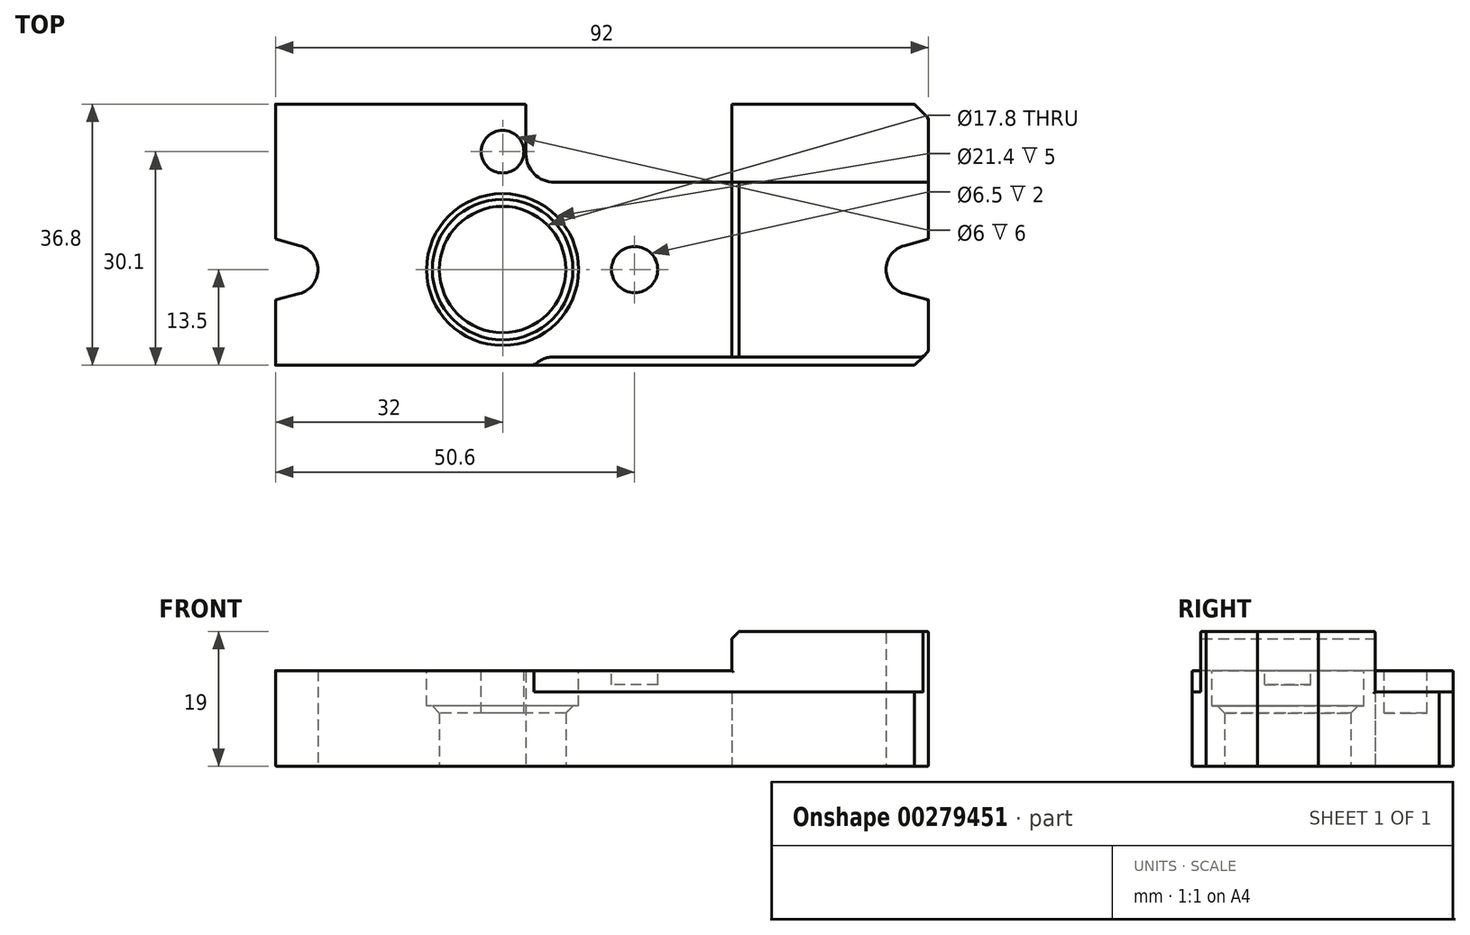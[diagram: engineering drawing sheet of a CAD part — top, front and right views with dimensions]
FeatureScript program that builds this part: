
annotation { "Feature Type Name" : "Feature", "Feature Type Description" : "" }
export const myFeature = defineFeature(function(context is Context, id is Id, definition is map)
    precondition{}
    {
        {
            var Q0;
            Q0=qCreatedBy(makeId("Top.planeOp"),FACE);
            var sketch = newSketch(context, id + "F0", { "sketchPlane" : qUnion([Q0])});
            skLineSegment(sketch, "E0", {"start": v(0, 0) * mm, "end": v(92, 0) * mm});
            skLineSegment(sketch, "E1", {"start": v(92, 0) * mm, "end": v(92, 9.2) * mm});
            skLineSegment(sketch, "E2", {"start": v(92, 36.8) * mm, "end": v(0, 36.8) * mm});
            skLineSegment(sketch, "E3", {"start": v(0, 36.8) * mm, "end": v(0, 17.8) * mm});
            skLineSegment(sketch, "E4", {"start": v(0, 0) * mm, "end": v(0, 9.2) * mm, "construction": true});
            skLineSegment(sketch, "E5", {"start": v(0, 13.5) * mm, "end": v(2.5, 13.5) * mm, "construction": true});
            skLineSegment(sketch, "E6", {"start": v(2.5, 13.5) * mm, "end": v(32, 13.5) * mm, "construction": true});
            skArc(sketch, "E7", {"start": v(3.4, 10.12) * mm, "mid": v(6, 13.5) * mm, "end": v(3.4, 16.88) * mm});
            skCircle(sketch, "E8", {"center": v(32, 13.5) * mm, "radius": 8.9 * mm});
            skCircle(sketch, "E9", {"center": v(32, 13.5) * mm, "radius": 10.7 * mm, "construction": true});
            skArc(sketch, "E10", {"start": v(18.3, 18.25) * mm, "mid": v(17.5, 13.5) * mm, "end": v(18.3, 8.75) * mm});
            skLineSegment(sketch, "E11", {"start": v(0, 0) * mm, "end": v(18.3, 0) * mm, "construction": true});
            skLineSegment(sketch, "E12", {"start": v(18.3, 0) * mm, "end": v(18.3, 8.75) * mm});
            skLineSegment(sketch, "E13.trimOffspring", {"start": v(18.3, 18.25) * mm, "end": v(18.3, 36.8) * mm});
            skLineSegment(sketch, "E14", {"start": v(3.4, 10.12) * mm, "end": v(0, 9.2) * mm});
            skLineSegment(sketch, "E15.MirrorCS", {"start": v(3.4, 16.88) * mm, "end": v(0, 17.8) * mm});
            skLineSegment(sketch, "E16.trimOffspring", {"start": v(0, 9.2) * mm, "end": v(0, 0) * mm});
            skLineSegment(sketch, "E17", {"start": v(32, 13.5) * mm, "end": v(89.5, 13.5) * mm, "construction": true});
            skArc(sketch, "E18", {"start": v(88.6, 16.88) * mm, "mid": v(86, 13.5) * mm, "end": v(88.6, 10.12) * mm});
            skLineSegment(sketch, "E19", {"start": v(88.6, 10.12) * mm, "end": v(92, 9.2) * mm});
            skLineSegment(sketch, "E20.MirrorCS", {"start": v(88.6, 16.88) * mm, "end": v(92, 17.8) * mm});
            skLineSegment(sketch, "E21.trimOffspring", {"start": v(92, 17.8) * mm, "end": v(92, 36.8) * mm});
            skLineSegment(sketch, "E22", {"start": v(0, 0) * mm, "end": v(50.6, 0) * mm, "construction": true});
            skLineSegment(sketch, "E23", {"start": v(50.6, 0) * mm, "end": v(50.6, 13.5) * mm, "construction": true});
            skCircle(sketch, "E24", {"center": v(50.6, 13.5) * mm, "radius": 3.25 * mm, "construction": true});
            skLineSegment(sketch, "E25", {"start": v(0, 0) * mm, "end": v(64.3, 0) * mm, "construction": true});
            skLineSegment(sketch, "E26", {"start": v(64.3, 0) * mm, "end": v(64.3, 36.8) * mm});
            skLineSegment(sketch, "E27", {"start": v(0, 0) * mm, "end": v(0, -2.8) * mm, "construction": true});
            skLineSegment(sketch, "E28", {"start": v(0, -2.8) * mm, "end": v(39.3, -2.8) * mm, "construction": true});
            skLineSegment(sketch, "E29", {"start": v(0, 0) * mm, "end": v(0, 1.2) * mm, "construction": true});
            skLineSegment(sketch, "E30", {"start": v(39.3, 1.2) * mm, "end": v(92, 1.2) * mm});
            skArc(sketch, "E31", {"start": v(39.3, 1.2) * mm, "mid": v(37.75, 0.89) * mm, "end": v(36.44, 0) * mm});
            skLineSegment(sketch, "E32.MirrorCS", {"start": v(39.3, 25.8) * mm, "end": v(92, 25.8) * mm});
            skArc(sketch, "E33.MirrorC", {"start": v(39.3, 25.8) * mm, "mid": v(36.47, 26.97) * mm, "end": v(35.3, 29.8) * mm});
            skLineSegment(sketch, "E34", {"start": v(35.3, 29.8) * mm, "end": v(35.3, 36.8) * mm});
            skPoint(sketch, "E35.orphan", {"position": v(0, 25.8) * mm});
            skLineSegment(sketch, "E36", {"start": v(32, 13.5) * mm, "end": v(32, 30.1) * mm, "construction": true});
            skCircle(sketch, "E37", {"center": v(32, 30.1) * mm, "radius": 3 * mm, "construction": true});
            skSolve(sketch);
        }
        {
            var Q0;
            Q0=qCreatedBy(makeId("Top.planeOp"),FACE);
            cPlane(context, id + "F1", {"entities" : qUnion([Q0]), "cplaneType" : CPlaneType.OFFSET, "offset" : 13.5 * mm, "width" : 150 * mm, "height" : 150 * mm});
        }
        {
            var Q0;
            Q0=qCreatedBy(id+"F1.planeOp",FACE);
            var sketch = newSketch(context, id + "F2", { "sketchPlane" : qUnion([Q0])});
            skCircle(sketch, "E38.0", {"center": v(32, 13.5) * mm, "radius": 10.7 * mm});
            skCircle(sketch, "E39.0", {"center": v(32, 30.1) * mm, "radius": 3 * mm});
            skCircle(sketch, "E40.0", {"center": v(50.6, 13.5) * mm, "radius": 3.25 * mm});
            skArc(sketch, "E41.0.0", {"start": v(18.3, 8.75) * mm, "mid": v(17.5, 13.5) * mm, "end": v(18.3, 18.25) * mm});
            skLineSegment(sketch, "E41.0.1", {"start": v(18.3, 18.25) * mm, "end": v(18.3, 36.8) * mm});
            skLineSegment(sketch, "E41.0.2", {"start": v(18.3, 36.8) * mm, "end": v(0, 36.8) * mm});
            skLineSegment(sketch, "E41.0.3", {"start": v(0, 36.8) * mm, "end": v(0, 17.8) * mm});
            skLineSegment(sketch, "E41.0.4", {"start": v(0, 17.8) * mm, "end": v(3.4, 16.88) * mm});
            skArc(sketch, "E41.0.5", {"start": v(3.4, 16.88) * mm, "mid": v(6, 13.5) * mm, "end": v(3.4, 10.12) * mm});
            skLineSegment(sketch, "E41.0.6", {"start": v(3.4, 10.12) * mm, "end": v(0, 9.2) * mm});
            skLineSegment(sketch, "E41.0.7", {"start": v(0, 9.2) * mm, "end": v(0, 0) * mm});
            skLineSegment(sketch, "E41.0.8", {"start": v(0, 0) * mm, "end": v(18.3, 0) * mm});
            skLineSegment(sketch, "E41.0.9", {"start": v(18.3, 0) * mm, "end": v(18.3, 8.75) * mm});
            skLineSegment(sketch, "E42.0.0", {"start": v(92, 25.8) * mm, "end": v(64.3, 25.8) * mm});
            skLineSegment(sketch, "E42.0.1", {"start": v(64.3, 25.8) * mm, "end": v(64.3, 1.2) * mm});
            skLineSegment(sketch, "E42.0.2", {"start": v(64.3, 1.2) * mm, "end": v(92, 1.2) * mm});
            skLineSegment(sketch, "E42.0.3", {"start": v(92, 1.2) * mm, "end": v(92, 9.2) * mm});
            skLineSegment(sketch, "E42.0.4", {"start": v(92, 9.2) * mm, "end": v(88.6, 10.12) * mm});
            skArc(sketch, "E42.0.5", {"start": v(88.6, 10.12) * mm, "mid": v(86, 13.5) * mm, "end": v(88.6, 16.88) * mm});
            skLineSegment(sketch, "E42.0.6", {"start": v(88.6, 16.88) * mm, "end": v(92, 17.8) * mm});
            skLineSegment(sketch, "E42.0.7", {"start": v(92, 17.8) * mm, "end": v(92, 25.8) * mm});
            skSolve(sketch);
        }
        {
            var Q0;
            {var subQ3=sQuery(id+"F0.wireOp",EDGE,"E3");Q0=makeQuery(id+"F0.imprint","IMPRINT",FACE,{"disambiguationData":[TD([[makeQuery(id+"F0.imprint","IMPRINT",EDGE,{"derivedFrom":subQ3}),1.0]])]});}
            var Q1;
            Q1=makeQuery(id+"F0.imprint","IMPRINT",FACE,{"disambiguationData":[TD([[makeQuery(id+"F0.imprint","IMPRINT",EDGE,{"derivedFrom":sQuery(id+"F0.wireOp",EDGE,"E8")}),-1.0]])]});
            var Q2;
            Q2=makeQuery(id+"F0.imprint","IMPRINT",FACE,{"disambiguationData":[TD([[makeQuery(id+"F0.imprint","IMPRINT",EDGE,{"derivedFrom":sQuery(id+"F0.wireOp",EDGE,"E18")}),-1.0]])]});
            extrude(context, id + "F3", {"entities" : qUnion([Q0, Q1, Q2]), "depth" : 13.5 * mm});
        }
        {
            var Q0;
            {var subQ0=sQuery(id+"F0.wireOp",EDGE,"E1");var subQ1=sQuery(id+"F0.wireOp",EDGE,"E0");var subQ2=makeQuery(id+"F0.imprint","INTERSECT",VERTEX,{"derivedFrom":[subQ1,subQ0]});Q0=makeQuery(id+"F0.imprint","IMPRINT",FACE,{"disambiguationData":[TD([[makeQuery(id+"F0.imprint","IMPRINT",EDGE,{"disambiguationData":[TD([[subQ2,1.0]])],"derivedFrom":subQ1}),1.0]])]});}
            var Q1;
            {var subQ3=sQuery(id+"F0.wireOp",EDGE,"E31");Q1=makeQuery(id+"F0.imprint","IMPRINT",FACE,{"disambiguationData":[TD([[makeQuery(id+"F0.imprint","IMPRINT",EDGE,{"derivedFrom":subQ3}),1.0]])]});}
            var Q2;
            {var subQ0=sQuery(id+"F0.wireOp",EDGE,"E33.MirrorC");Q2=makeQuery(id+"F0.imprint","IMPRINT",FACE,{"disambiguationData":[TD([[makeQuery(id+"F0.imprint","IMPRINT",EDGE,{"derivedFrom":subQ0}),-1.0]])]});}
            var Q3;
            {var subQ0=sQuery(id+"F0.wireOp",EDGE,"E21.trimOffspring");var subQ1=sQuery(id+"F0.wireOp",EDGE,"E2");var subQ2=makeQuery(id+"F0.imprint","INTERSECT",VERTEX,{"derivedFrom":[subQ1,subQ0]});Q3=makeQuery(id+"F0.imprint","IMPRINT",FACE,{"disambiguationData":[TD([[makeQuery(id+"F0.imprint","IMPRINT",EDGE,{"disambiguationData":[TD([[subQ2,-1.0]])],"derivedFrom":subQ1}),1.0]])]});}
            extrude(context, id + "F4", {"entities" : qUnion([Q0, Q1, Q2, Q3]), "operationType" : NewBodyOperationType.ADD, "depth" : 10.5 * mm});
        }
        {
            var Q0;
            Q0=makeQuery(id+"F2.imprint","IMPRINT",FACE,{"disambiguationData":[TD([[makeQuery(id+"F2.imprint","IMPRINT",EDGE,{"derivedFrom":sQuery(id+"F2.wireOp",EDGE,"E38.0")}),1.0]])]});
            extrude(context, id + "F5", {"entities" : qUnion([Q0]), "operationType" : NewBodyOperationType.REMOVE, "oppositeDirection" : true, "depth" : 5 * mm});
        }
        {
            var Q0;
            Q0=makeQuery(id+"F2.imprint","IMPRINT",FACE,{"disambiguationData":[TD([[makeQuery(id+"F2.imprint","IMPRINT",EDGE,{"derivedFrom":sQuery(id+"F2.wireOp",EDGE,"E40.0")}),1.0]])]});
            extrude(context, id + "F6", {"entities" : qUnion([Q0]), "operationType" : NewBodyOperationType.REMOVE, "oppositeDirection" : true, "depth" : 2 * mm});
        }
        {
            var Q0;
            Q0=makeQuery(id+"F2.imprint","IMPRINT",FACE,{"disambiguationData":[TD([[makeQuery(id+"F2.imprint","IMPRINT",EDGE,{"derivedFrom":sQuery(id+"F2.wireOp",EDGE,"E39.0")}),1.0]])]});
            extrude(context, id + "F7", {"entities" : qUnion([Q0]), "operationType" : NewBodyOperationType.REMOVE, "oppositeDirection" : true, "depth" : 6 * mm});
        }
        {
            var Q0;
            Q0=makeQuery(id+"F2.imprint","IMPRINT",FACE,{"disambiguationData":[TD([[makeQuery(id+"F2.imprint","IMPRINT",EDGE,{"derivedFrom":sQuery(id+"F2.wireOp",EDGE,"E41.0.0")}),1.0]])]});
            var Q1;
            Q1=makeQuery(id+"F2.imprint","IMPRINT",FACE,{"disambiguationData":[TD([[makeQuery(id+"F2.imprint","IMPRINT",EDGE,{"derivedFrom":sQuery(id+"F2.wireOp",EDGE,"E42.0.0")}),1.0]])]});
            extrude(context, id + "F8", {"entities" : qUnion([Q0, Q1]), "operationType" : NewBodyOperationType.ADD, "depth" : 5.5 * mm});
        }
        {
            var Q0;
            Q0=makeQuery(id+"F5.boolean.opBoolean","INTERSECT",EDGE,{"derivedFrom":[makeQuery(id+"F3.opExtrude","SWEPT_FACE",FACE,{"disambiguationData":[OSD([sQuery(id+"F0.wireOp",EDGE,"E8")])]}),makeQuery(id+"F5.opExtrude","CAP_FACE",FACE,{"disambiguationData":[OSD([sQuery(id+"F2.wireOp",EDGE,"E38.0")])],"isStart":false})]});
            var Q1;
            Q1=makeQuery(id+"F8.opExtrude","CAP_EDGE",EDGE,{"disambiguationData":[OSD([sQuery(id+"F2.wireOp",EDGE,"E41.0.1")])],"isStart":false});
            var Q2;
            Q2=makeQuery(id+"F8.opExtrude","CAP_EDGE",EDGE,{"disambiguationData":[OSD([sQuery(id+"F2.wireOp",EDGE,"E42.0.1")])],"isStart":false});
            chamfer(context, id + "F9", {"entities" : qUnion([Q0, Q1, Q2]), "width" : 1 * mm, "tangentPropagation" : true});
        }
        {
            var Q0;
            Q0=makeQuery(id+"F4.opExtrude","SWEPT_EDGE",EDGE,{"disambiguationData":[OSD([sQuery(id+"F0.wireOp",EDGE,"E0"),sQuery(id+"F0.wireOp",EDGE,"E1")])]});
            var Q1;
            Q1=makeQuery(id+"F4.opExtrude","SWEPT_EDGE",EDGE,{"disambiguationData":[OSD([sQuery(id+"F0.wireOp",EDGE,"E2"),sQuery(id+"F0.wireOp",EDGE,"E21.trimOffspring")])]});
            var Q2;
            Q2=makeQuery(id+"F8.boolean.opBoolean","MERGE",EDGE,{"derivedFrom":[makeQuery(id+"F3.opExtrude","SWEPT_EDGE",EDGE,{"disambiguationData":[OSD([sQuery(id+"F0.wireOp",EDGE,"E2"),sQuery(id+"F0.wireOp",EDGE,"E3")])]}),makeQuery(id+"F8.opExtrude","SWEPT_EDGE",EDGE,{"disambiguationData":[OSD([sQuery(id+"F2.wireOp",EDGE,"E41.0.2"),sQuery(id+"F2.wireOp",EDGE,"E41.0.3")])]})]});
            var Q3;
            Q3=makeQuery(id+"F8.boolean.opBoolean","MERGE",EDGE,{"derivedFrom":[makeQuery(id+"F3.opExtrude","SWEPT_EDGE",EDGE,{"disambiguationData":[OSD([sQuery(id+"F0.wireOp",EDGE,"E0"),sQuery(id+"F0.wireOp",EDGE,"E16.trimOffspring")])]}),makeQuery(id+"F8.opExtrude","SWEPT_EDGE",EDGE,{"disambiguationData":[OSD([sQuery(id+"F2.wireOp",EDGE,"E41.0.7"),sQuery(id+"F2.wireOp",EDGE,"E41.0.8")])]})]});
            chamfer(context, id + "F10", {"entities" : qUnion([Q0, Q1, Q2, Q3]), "width" : 2 * mm, "tangentPropagation" : true});
        }
        {
            var Q0;
            {var subQ0=sQuery(id+"F2.wireOp",EDGE,"E41.0.8");var subQ1=sQuery(id+"F2.wireOp",EDGE,"E41.0.7");Q0=makeQuery(id+"F10.opChamfer","BLEND_EDGE",EDGE,{"blendedFrom":[makeQuery(id+"F8.boolean.opBoolean","MERGE",EDGE,{"derivedFrom":[makeQuery(id+"F3.opExtrude","SWEPT_EDGE",EDGE,{"disambiguationData":[OSD([sQuery(id+"F0.wireOp",EDGE,"E0"),sQuery(id+"F0.wireOp",EDGE,"E16.trimOffspring")])]}),makeQuery(id+"F8.opExtrude","SWEPT_EDGE",EDGE,{"disambiguationData":[OSD([subQ1,subQ0])]})]}),makeQuery(id+"F8.opExtrude","CAP_FACE",FACE,{"disambiguationData":[OSD([sQuery(id+"F2.wireOp",EDGE,"E41.0.0"),sQuery(id+"F2.wireOp",EDGE,"E41.0.1"),sQuery(id+"F2.wireOp",EDGE,"E41.0.2"),sQuery(id+"F2.wireOp",EDGE,"E41.0.3"),sQuery(id+"F2.wireOp",EDGE,"E41.0.4"),sQuery(id+"F2.wireOp",EDGE,"E41.0.5"),sQuery(id+"F2.wireOp",EDGE,"E41.0.6"),subQ1,subQ0,sQuery(id+"F2.wireOp",EDGE,"E41.0.9")])],"isStart":false})],"blendedInto":[makeQuery(id+"F8.opExtrude","CAP_FACE",FACE,{"disambiguationData":[OSD([sQuery(id+"F2.wireOp",EDGE,"E41.0.0"),sQuery(id+"F2.wireOp",EDGE,"E41.0.1"),sQuery(id+"F2.wireOp",EDGE,"E41.0.2"),sQuery(id+"F2.wireOp",EDGE,"E41.0.3"),sQuery(id+"F2.wireOp",EDGE,"E41.0.4"),sQuery(id+"F2.wireOp",EDGE,"E41.0.5"),sQuery(id+"F2.wireOp",EDGE,"E41.0.6"),subQ1,subQ0,sQuery(id+"F2.wireOp",EDGE,"E41.0.9")])],"isStart":false})]});}
            var Q1;
            Q1=makeQuery(id+"F8.opExtrude","CAP_EDGE",EDGE,{"disambiguationData":[OSD([sQuery(id+"F2.wireOp",EDGE,"E41.0.7")])],"isStart":false});
            var Q2;
            Q2=makeQuery(id+"F8.opExtrude","CAP_EDGE",EDGE,{"disambiguationData":[OSD([sQuery(id+"F2.wireOp",EDGE,"E41.0.6")])],"isStart":false});
            var Q3;
            Q3=makeQuery(id+"F8.opExtrude","CAP_EDGE",EDGE,{"disambiguationData":[OSD([sQuery(id+"F2.wireOp",EDGE,"E41.0.5")])],"isStart":false});
            var Q4;
            Q4=makeQuery(id+"F8.opExtrude","CAP_EDGE",EDGE,{"disambiguationData":[OSD([sQuery(id+"F2.wireOp",EDGE,"E41.0.3")])],"isStart":false});
            var Q5;
            Q5=makeQuery(id+"F8.opExtrude","CAP_EDGE",EDGE,{"disambiguationData":[OSD([sQuery(id+"F2.wireOp",EDGE,"E41.0.4")])],"isStart":false});
            var Q6;
            {var subQ0=sQuery(id+"F2.wireOp",EDGE,"E41.0.3");var subQ1=sQuery(id+"F2.wireOp",EDGE,"E41.0.2");Q6=makeQuery(id+"F10.opChamfer","BLEND_EDGE",EDGE,{"blendedFrom":[makeQuery(id+"F8.boolean.opBoolean","MERGE",EDGE,{"derivedFrom":[makeQuery(id+"F3.opExtrude","SWEPT_EDGE",EDGE,{"disambiguationData":[OSD([sQuery(id+"F0.wireOp",EDGE,"E2"),sQuery(id+"F0.wireOp",EDGE,"E3")])]}),makeQuery(id+"F8.opExtrude","SWEPT_EDGE",EDGE,{"disambiguationData":[OSD([subQ1,subQ0])]})]}),makeQuery(id+"F8.opExtrude","CAP_FACE",FACE,{"disambiguationData":[OSD([sQuery(id+"F2.wireOp",EDGE,"E41.0.0"),sQuery(id+"F2.wireOp",EDGE,"E41.0.1"),subQ1,subQ0,sQuery(id+"F2.wireOp",EDGE,"E41.0.4"),sQuery(id+"F2.wireOp",EDGE,"E41.0.5"),sQuery(id+"F2.wireOp",EDGE,"E41.0.6"),sQuery(id+"F2.wireOp",EDGE,"E41.0.7"),sQuery(id+"F2.wireOp",EDGE,"E41.0.8"),sQuery(id+"F2.wireOp",EDGE,"E41.0.9")])],"isStart":false})],"blendedInto":[makeQuery(id+"F8.opExtrude","CAP_FACE",FACE,{"disambiguationData":[OSD([sQuery(id+"F2.wireOp",EDGE,"E41.0.0"),sQuery(id+"F2.wireOp",EDGE,"E41.0.1"),subQ1,subQ0,sQuery(id+"F2.wireOp",EDGE,"E41.0.4"),sQuery(id+"F2.wireOp",EDGE,"E41.0.5"),sQuery(id+"F2.wireOp",EDGE,"E41.0.6"),sQuery(id+"F2.wireOp",EDGE,"E41.0.7"),sQuery(id+"F2.wireOp",EDGE,"E41.0.8"),sQuery(id+"F2.wireOp",EDGE,"E41.0.9")])],"isStart":false})]});}
            var Q7;
            Q7=makeQuery(id+"F8.opExtrude","CAP_EDGE",EDGE,{"disambiguationData":[OSD([sQuery(id+"F2.wireOp",EDGE,"E41.0.2")])],"isStart":false});
            var Q8;
            {var subQ0=sQuery(id+"F0.wireOp",EDGE,"E2");Q8=makeQuery(id+"F9.opChamfer","BLEND_EDGE",EDGE,{"blendedFrom":[makeQuery(id+"F8.opExtrude","CAP_EDGE",EDGE,{"disambiguationData":[OSD([sQuery(id+"F2.wireOp",EDGE,"E41.0.1")])],"isStart":false}),makeQuery(id+"F8.boolean.opBoolean","MERGE",FACE,{"derivedFrom":[makeQuery(id+"F4.boolean.opBoolean","MERGE",FACE,{"derivedFrom":[makeQuery(id+"F3.opExtrude","SWEPT_FACE",FACE,{"disambiguationData":[OSD([subQ0])]}),makeQuery(id+"F4.opExtrude","SWEPT_FACE",FACE,{"disambiguationData":[OSD([subQ0])]})]}),makeQuery(id+"F8.opExtrude","SWEPT_FACE",FACE,{"disambiguationData":[OSD([sQuery(id+"F2.wireOp",EDGE,"E41.0.2")])]})]})],"blendedInto":[makeQuery(id+"F8.boolean.opBoolean","MERGE",FACE,{"derivedFrom":[makeQuery(id+"F4.boolean.opBoolean","MERGE",FACE,{"derivedFrom":[makeQuery(id+"F3.opExtrude","SWEPT_FACE",FACE,{"disambiguationData":[OSD([subQ0])]}),makeQuery(id+"F4.opExtrude","SWEPT_FACE",FACE,{"disambiguationData":[OSD([subQ0])]})]}),makeQuery(id+"F8.opExtrude","SWEPT_FACE",FACE,{"disambiguationData":[OSD([sQuery(id+"F2.wireOp",EDGE,"E41.0.2")])]})]})]});}
            var Q9;
            Q9=makeQuery(id+"F8.opExtrude","SWEPT_EDGE",EDGE,{"disambiguationData":[OSD([sQuery(id+"F2.wireOp",EDGE,"E41.0.1"),sQuery(id+"F2.wireOp",EDGE,"E41.0.2")])]});
            var Q10;
            Q10=makeQuery(id+"F3.opExtrude","CAP_EDGE",EDGE,{"disambiguationData":[OSD([sQuery(id+"F0.wireOp",EDGE,"E2")])],"isStart":false});
            var Q11;
            Q11=makeQuery(id+"F3.opExtrude","SWEPT_EDGE",EDGE,{"disambiguationData":[OSD([sQuery(id+"F0.wireOp",EDGE,"E2"),sQuery(id+"F0.wireOp",EDGE,"E34")])]});
            var Q12;
            Q12=makeQuery(id+"F4.opExtrude","CAP_EDGE",EDGE,{"disambiguationData":[OSD([sQuery(id+"F0.wireOp",EDGE,"E2")])],"isStart":false});
            var Q13;
            {var subQ0=sQuery(id+"F0.wireOp",EDGE,"E21.trimOffspring");var subQ1=sQuery(id+"F0.wireOp",EDGE,"E2");Q13=makeQuery(id+"F10.opChamfer","BLEND_EDGE",EDGE,{"blendedFrom":[makeQuery(id+"F4.opExtrude","SWEPT_EDGE",EDGE,{"disambiguationData":[OSD([subQ1,subQ0])]}),makeQuery(id+"F4.opExtrude","CAP_FACE",FACE,{"disambiguationData":[OSD([subQ1,subQ0,sQuery(id+"F0.wireOp",EDGE,"E32.MirrorCS"),sQuery(id+"F0.wireOp",EDGE,"E33.MirrorC"),sQuery(id+"F0.wireOp",EDGE,"E34")])],"isStart":false})],"blendedInto":[makeQuery(id+"F4.opExtrude","CAP_FACE",FACE,{"disambiguationData":[OSD([subQ1,subQ0,sQuery(id+"F0.wireOp",EDGE,"E32.MirrorCS"),sQuery(id+"F0.wireOp",EDGE,"E33.MirrorC"),sQuery(id+"F0.wireOp",EDGE,"E34")])],"isStart":false})]});}
            var Q14;
            Q14=makeQuery(id+"F4.opExtrude","CAP_EDGE",EDGE,{"disambiguationData":[OSD([sQuery(id+"F0.wireOp",EDGE,"E21.trimOffspring")])],"isStart":false});
            var Q15;
            Q15=makeQuery(id+"F8.boolean.opBoolean","MERGE",EDGE,{"derivedFrom":[makeQuery(id+"F3.opExtrude","SWEPT_EDGE",EDGE,{"disambiguationData":[OSD([sQuery(id+"F0.wireOp",EDGE,"E21.trimOffspring"),sQuery(id+"F0.wireOp",EDGE,"E32.MirrorCS")])]}),makeQuery(id+"F8.opExtrude","SWEPT_EDGE",EDGE,{"disambiguationData":[OSD([sQuery(id+"F2.wireOp",EDGE,"E42.0.0"),sQuery(id+"F2.wireOp",EDGE,"E42.0.7")])]})]});
            var Q16;
            Q16=makeQuery(id+"F8.opExtrude","CAP_EDGE",EDGE,{"disambiguationData":[OSD([sQuery(id+"F2.wireOp",EDGE,"E42.0.0")])],"isStart":false});
            var Q17;
            Q17=makeQuery(id+"F8.opExtrude","CAP_EDGE",EDGE,{"disambiguationData":[OSD([sQuery(id+"F2.wireOp",EDGE,"E42.0.2")])],"isStart":false});
            var Q18;
            Q18=makeQuery(id+"F10.opChamfer","BLEND_EDGE",EDGE,{"blendedFrom":[makeQuery(id+"F4.opExtrude","SWEPT_EDGE",EDGE,{"disambiguationData":[OSD([sQuery(id+"F0.wireOp",EDGE,"E0"),sQuery(id+"F0.wireOp",EDGE,"E1")])]}),makeQuery(id+"F8.opExtrude","CAP_FACE",FACE,{"disambiguationData":[OSD([sQuery(id+"F2.wireOp",EDGE,"E42.0.0"),sQuery(id+"F2.wireOp",EDGE,"E42.0.1"),sQuery(id+"F2.wireOp",EDGE,"E42.0.2"),sQuery(id+"F2.wireOp",EDGE,"E42.0.3"),sQuery(id+"F2.wireOp",EDGE,"E42.0.4"),sQuery(id+"F2.wireOp",EDGE,"E42.0.5"),sQuery(id+"F2.wireOp",EDGE,"E42.0.6"),sQuery(id+"F2.wireOp",EDGE,"E42.0.7")])],"isStart":false})],"blendedInto":[makeQuery(id+"F8.opExtrude","CAP_FACE",FACE,{"disambiguationData":[OSD([sQuery(id+"F2.wireOp",EDGE,"E42.0.0"),sQuery(id+"F2.wireOp",EDGE,"E42.0.1"),sQuery(id+"F2.wireOp",EDGE,"E42.0.2"),sQuery(id+"F2.wireOp",EDGE,"E42.0.3"),sQuery(id+"F2.wireOp",EDGE,"E42.0.4"),sQuery(id+"F2.wireOp",EDGE,"E42.0.5"),sQuery(id+"F2.wireOp",EDGE,"E42.0.6"),sQuery(id+"F2.wireOp",EDGE,"E42.0.7")])],"isStart":false})]});
            var Q19;
            Q19=makeQuery(id+"F8.opExtrude","CAP_EDGE",EDGE,{"disambiguationData":[OSD([sQuery(id+"F2.wireOp",EDGE,"E42.0.3")])],"isStart":false});
            var Q20;
            Q20=makeQuery(id+"F8.opExtrude","CAP_EDGE",EDGE,{"disambiguationData":[OSD([sQuery(id+"F2.wireOp",EDGE,"E42.0.4")])],"isStart":false});
            var Q21;
            Q21=makeQuery(id+"F8.opExtrude","CAP_EDGE",EDGE,{"disambiguationData":[OSD([sQuery(id+"F2.wireOp",EDGE,"E42.0.5")])],"isStart":false});
            var Q22;
            Q22=makeQuery(id+"F8.opExtrude","CAP_EDGE",EDGE,{"disambiguationData":[OSD([sQuery(id+"F2.wireOp",EDGE,"E42.0.7")])],"isStart":false});
            var Q23;
            Q23=makeQuery(id+"F8.opExtrude","SWEPT_EDGE",EDGE,{"disambiguationData":[OSD([sQuery(id+"F2.wireOp",EDGE,"E42.0.1"),sQuery(id+"F2.wireOp",EDGE,"E42.0.2")])]});
            var Q24;
            Q24=makeQuery(id+"F3.opExtrude","CAP_EDGE",EDGE,{"disambiguationData":[OSD([sQuery(id+"F0.wireOp",EDGE,"E30")])],"isStart":false});
            var Q25;
            Q25=makeQuery(id+"F3.opExtrude","CAP_EDGE",EDGE,{"disambiguationData":[OSD([sQuery(id+"F0.wireOp",EDGE,"E0")])],"isStart":false});
            var Q26;
            Q26=makeQuery(id+"F8.opExtrude","SWEPT_EDGE",EDGE,{"disambiguationData":[OSD([sQuery(id+"F2.wireOp",EDGE,"E41.0.8"),sQuery(id+"F2.wireOp",EDGE,"E41.0.9")])]});
            var Q27;
            {var subQ0=sQuery(id+"F0.wireOp",EDGE,"E0");Q27=makeQuery(id+"F9.opChamfer","BLEND_EDGE",EDGE,{"blendedFrom":[makeQuery(id+"F8.opExtrude","CAP_EDGE",EDGE,{"disambiguationData":[OSD([sQuery(id+"F2.wireOp",EDGE,"E41.0.1")])],"isStart":false}),makeQuery(id+"F8.boolean.opBoolean","MERGE",FACE,{"derivedFrom":[makeQuery(id+"F4.boolean.opBoolean","MERGE",FACE,{"derivedFrom":[makeQuery(id+"F3.opExtrude","SWEPT_FACE",FACE,{"disambiguationData":[OSD([subQ0])]}),makeQuery(id+"F4.opExtrude","SWEPT_FACE",FACE,{"disambiguationData":[OSD([subQ0])]})]}),makeQuery(id+"F8.opExtrude","SWEPT_FACE",FACE,{"disambiguationData":[OSD([sQuery(id+"F2.wireOp",EDGE,"E41.0.8")])]})]})],"blendedInto":[makeQuery(id+"F8.boolean.opBoolean","MERGE",FACE,{"derivedFrom":[makeQuery(id+"F4.boolean.opBoolean","MERGE",FACE,{"derivedFrom":[makeQuery(id+"F3.opExtrude","SWEPT_FACE",FACE,{"disambiguationData":[OSD([subQ0])]}),makeQuery(id+"F4.opExtrude","SWEPT_FACE",FACE,{"disambiguationData":[OSD([subQ0])]})]}),makeQuery(id+"F8.opExtrude","SWEPT_FACE",FACE,{"disambiguationData":[OSD([sQuery(id+"F2.wireOp",EDGE,"E41.0.8")])]})]})]});}
            var Q28;
            Q28=makeQuery(id+"F8.opExtrude","CAP_EDGE",EDGE,{"disambiguationData":[OSD([sQuery(id+"F2.wireOp",EDGE,"E41.0.8")])],"isStart":false});
            var Q29;
            Q29=makeQuery(id+"F8.opExtrude","SWEPT_EDGE",EDGE,{"disambiguationData":[OSD([sQuery(id+"F2.wireOp",EDGE,"E42.0.0"),sQuery(id+"F2.wireOp",EDGE,"E42.0.1")])]});
            var Q30;
            Q30=makeQuery(id+"F9.opChamfer","BLEND_EDGE",EDGE,{"blendedFrom":[makeQuery(id+"F8.opExtrude","CAP_EDGE",EDGE,{"disambiguationData":[OSD([sQuery(id+"F2.wireOp",EDGE,"E42.0.1")])],"isStart":false}),makeQuery(id+"F8.boolean.opBoolean","MERGE",FACE,{"derivedFrom":[makeQuery(id+"F3.opExtrude","SWEPT_FACE",FACE,{"disambiguationData":[OSD([sQuery(id+"F0.wireOp",EDGE,"E32.MirrorCS")])]}),makeQuery(id+"F8.opExtrude","SWEPT_FACE",FACE,{"disambiguationData":[OSD([sQuery(id+"F2.wireOp",EDGE,"E42.0.0")])]})]})],"blendedInto":[makeQuery(id+"F8.boolean.opBoolean","MERGE",FACE,{"derivedFrom":[makeQuery(id+"F3.opExtrude","SWEPT_FACE",FACE,{"disambiguationData":[OSD([sQuery(id+"F0.wireOp",EDGE,"E32.MirrorCS")])]}),makeQuery(id+"F8.opExtrude","SWEPT_FACE",FACE,{"disambiguationData":[OSD([sQuery(id+"F2.wireOp",EDGE,"E42.0.0")])]})]})]});
            var Q31;
            Q31=makeQuery(id+"F3.opExtrude","CAP_EDGE",EDGE,{"disambiguationData":[OSD([sQuery(id+"F0.wireOp",EDGE,"E32.MirrorCS")])],"isStart":false});
            var Q32;
            Q32=makeQuery(id+"F3.opExtrude","CAP_EDGE",EDGE,{"disambiguationData":[OSD([sQuery(id+"F0.wireOp",EDGE,"E33.MirrorC")])],"isStart":false});
            var Q33;
            Q33=makeQuery(id+"F3.opExtrude","CAP_EDGE",EDGE,{"disambiguationData":[OSD([sQuery(id+"F0.wireOp",EDGE,"E34")])],"isStart":false});
            var Q34;
            {var subQ0=sQuery(id+"F0.wireOp",EDGE,"E2");Q34=makeQuery(id+"F4.boolean.opBoolean","MERGE",EDGE,{"derivedFrom":[makeQuery(id+"F3.opExtrude","CAP_EDGE",EDGE,{"disambiguationData":[OSD([subQ0])],"isStart":true}),makeQuery(id+"F4.opExtrude","CAP_EDGE",EDGE,{"disambiguationData":[OSD([subQ0])],"isStart":true})]});}
            var Q35;
            {var subQ0=sQuery(id+"F0.wireOp",EDGE,"E34");var subQ1=sQuery(id+"F0.wireOp",EDGE,"E33.MirrorC");var subQ2=sQuery(id+"F0.wireOp",EDGE,"E32.MirrorCS");var subQ3=sQuery(id+"F0.wireOp",EDGE,"E21.trimOffspring");var subQ4=sQuery(id+"F0.wireOp",EDGE,"E2");var subQ5=sQuery(id+"F0.wireOp",EDGE,"E31");var subQ6=sQuery(id+"F0.wireOp",EDGE,"E30");var subQ7=sQuery(id+"F0.wireOp",EDGE,"E1");var subQ8=sQuery(id+"F0.wireOp",EDGE,"E0");Q35=makeQuery(id+"F10.opChamfer","BLEND_EDGE",EDGE,{"blendedFrom":[makeQuery(id+"F4.opExtrude","SWEPT_EDGE",EDGE,{"disambiguationData":[OSD([subQ4,subQ3])]}),makeQuery(id+"F4.boolean.opBoolean","MERGE",FACE,{"derivedFrom":[makeQuery(id+"F3.opExtrude","CAP_FACE",FACE,{"disambiguationData":[OSD([subQ8,subQ7,subQ4,sQuery(id+"F0.wireOp",EDGE,"E3"),sQuery(id+"F0.wireOp",EDGE,"E7"),sQuery(id+"F0.wireOp",EDGE,"E8"),sQuery(id+"F0.wireOp",EDGE,"E14"),sQuery(id+"F0.wireOp",EDGE,"E15.MirrorCS"),sQuery(id+"F0.wireOp",EDGE,"E16.trimOffspring"),sQuery(id+"F0.wireOp",EDGE,"E18"),sQuery(id+"F0.wireOp",EDGE,"E19"),sQuery(id+"F0.wireOp",EDGE,"E20.MirrorCS"),subQ3,subQ6,subQ5,subQ2,subQ1,subQ0])],"isStart":true}),makeQuery(id+"F4.opExtrude","CAP_FACE",FACE,{"disambiguationData":[OSD([subQ8,subQ7,subQ6,subQ5])],"isStart":true}),makeQuery(id+"F4.opExtrude","CAP_FACE",FACE,{"disambiguationData":[OSD([subQ4,subQ3,subQ2,subQ1,subQ0])],"isStart":true})]})],"blendedInto":[makeQuery(id+"F4.boolean.opBoolean","MERGE",FACE,{"derivedFrom":[makeQuery(id+"F3.opExtrude","CAP_FACE",FACE,{"disambiguationData":[OSD([subQ8,subQ7,subQ4,sQuery(id+"F0.wireOp",EDGE,"E3"),sQuery(id+"F0.wireOp",EDGE,"E7"),sQuery(id+"F0.wireOp",EDGE,"E8"),sQuery(id+"F0.wireOp",EDGE,"E14"),sQuery(id+"F0.wireOp",EDGE,"E15.MirrorCS"),sQuery(id+"F0.wireOp",EDGE,"E16.trimOffspring"),sQuery(id+"F0.wireOp",EDGE,"E18"),sQuery(id+"F0.wireOp",EDGE,"E19"),sQuery(id+"F0.wireOp",EDGE,"E20.MirrorCS"),subQ3,subQ6,subQ5,subQ2,subQ1,subQ0])],"isStart":true}),makeQuery(id+"F4.opExtrude","CAP_FACE",FACE,{"disambiguationData":[OSD([subQ8,subQ7,subQ6,subQ5])],"isStart":true}),makeQuery(id+"F4.opExtrude","CAP_FACE",FACE,{"disambiguationData":[OSD([subQ4,subQ3,subQ2,subQ1,subQ0])],"isStart":true})]})]});}
            var Q36;
            {var subQ0=sQuery(id+"F0.wireOp",EDGE,"E21.trimOffspring");Q36=makeQuery(id+"F4.boolean.opBoolean","MERGE",EDGE,{"derivedFrom":[makeQuery(id+"F3.opExtrude","CAP_EDGE",EDGE,{"disambiguationData":[OSD([subQ0])],"isStart":true}),makeQuery(id+"F4.opExtrude","CAP_EDGE",EDGE,{"disambiguationData":[OSD([subQ0])],"isStart":true})]});}
            var Q37;
            Q37=makeQuery(id+"F3.opExtrude","CAP_EDGE",EDGE,{"disambiguationData":[OSD([sQuery(id+"F0.wireOp",EDGE,"E20.MirrorCS")])],"isStart":true});
            var Q38;
            Q38=makeQuery(id+"F3.opExtrude","CAP_EDGE",EDGE,{"disambiguationData":[OSD([sQuery(id+"F0.wireOp",EDGE,"E18")])],"isStart":true});
            var Q39;
            {var subQ0=sQuery(id+"F0.wireOp",EDGE,"E1");Q39=makeQuery(id+"F4.boolean.opBoolean","MERGE",EDGE,{"derivedFrom":[makeQuery(id+"F3.opExtrude","CAP_EDGE",EDGE,{"disambiguationData":[OSD([subQ0])],"isStart":true}),makeQuery(id+"F4.opExtrude","CAP_EDGE",EDGE,{"disambiguationData":[OSD([subQ0])],"isStart":true})]});}
            var Q40;
            {var subQ0=sQuery(id+"F0.wireOp",EDGE,"E34");var subQ1=sQuery(id+"F0.wireOp",EDGE,"E33.MirrorC");var subQ2=sQuery(id+"F0.wireOp",EDGE,"E32.MirrorCS");var subQ3=sQuery(id+"F0.wireOp",EDGE,"E21.trimOffspring");var subQ4=sQuery(id+"F0.wireOp",EDGE,"E2");var subQ5=sQuery(id+"F0.wireOp",EDGE,"E31");var subQ6=sQuery(id+"F0.wireOp",EDGE,"E30");var subQ7=sQuery(id+"F0.wireOp",EDGE,"E1");var subQ8=sQuery(id+"F0.wireOp",EDGE,"E0");Q40=makeQuery(id+"F10.opChamfer","BLEND_EDGE",EDGE,{"blendedFrom":[makeQuery(id+"F4.opExtrude","SWEPT_EDGE",EDGE,{"disambiguationData":[OSD([subQ8,subQ7])]}),makeQuery(id+"F4.boolean.opBoolean","MERGE",FACE,{"derivedFrom":[makeQuery(id+"F3.opExtrude","CAP_FACE",FACE,{"disambiguationData":[OSD([subQ8,subQ7,subQ4,sQuery(id+"F0.wireOp",EDGE,"E3"),sQuery(id+"F0.wireOp",EDGE,"E7"),sQuery(id+"F0.wireOp",EDGE,"E8"),sQuery(id+"F0.wireOp",EDGE,"E14"),sQuery(id+"F0.wireOp",EDGE,"E15.MirrorCS"),sQuery(id+"F0.wireOp",EDGE,"E16.trimOffspring"),sQuery(id+"F0.wireOp",EDGE,"E18"),sQuery(id+"F0.wireOp",EDGE,"E19"),sQuery(id+"F0.wireOp",EDGE,"E20.MirrorCS"),subQ3,subQ6,subQ5,subQ2,subQ1,subQ0])],"isStart":true}),makeQuery(id+"F4.opExtrude","CAP_FACE",FACE,{"disambiguationData":[OSD([subQ8,subQ7,subQ6,subQ5])],"isStart":true}),makeQuery(id+"F4.opExtrude","CAP_FACE",FACE,{"disambiguationData":[OSD([subQ4,subQ3,subQ2,subQ1,subQ0])],"isStart":true})]})],"blendedInto":[makeQuery(id+"F4.boolean.opBoolean","MERGE",FACE,{"derivedFrom":[makeQuery(id+"F3.opExtrude","CAP_FACE",FACE,{"disambiguationData":[OSD([subQ8,subQ7,subQ4,sQuery(id+"F0.wireOp",EDGE,"E3"),sQuery(id+"F0.wireOp",EDGE,"E7"),sQuery(id+"F0.wireOp",EDGE,"E8"),sQuery(id+"F0.wireOp",EDGE,"E14"),sQuery(id+"F0.wireOp",EDGE,"E15.MirrorCS"),sQuery(id+"F0.wireOp",EDGE,"E16.trimOffspring"),sQuery(id+"F0.wireOp",EDGE,"E18"),sQuery(id+"F0.wireOp",EDGE,"E19"),sQuery(id+"F0.wireOp",EDGE,"E20.MirrorCS"),subQ3,subQ6,subQ5,subQ2,subQ1,subQ0])],"isStart":true}),makeQuery(id+"F4.opExtrude","CAP_FACE",FACE,{"disambiguationData":[OSD([subQ8,subQ7,subQ6,subQ5])],"isStart":true}),makeQuery(id+"F4.opExtrude","CAP_FACE",FACE,{"disambiguationData":[OSD([subQ4,subQ3,subQ2,subQ1,subQ0])],"isStart":true})]})]});}
            var Q41;
            {var subQ0=sQuery(id+"F0.wireOp",EDGE,"E0");Q41=makeQuery(id+"F4.boolean.opBoolean","MERGE",EDGE,{"derivedFrom":[makeQuery(id+"F3.opExtrude","CAP_EDGE",EDGE,{"disambiguationData":[OSD([subQ0])],"isStart":true}),makeQuery(id+"F4.opExtrude","CAP_EDGE",EDGE,{"disambiguationData":[OSD([subQ0])],"isStart":true})]});}
            var Q42;
            {var subQ0=sQuery(id+"F0.wireOp",EDGE,"E34");var subQ1=sQuery(id+"F0.wireOp",EDGE,"E33.MirrorC");var subQ2=sQuery(id+"F0.wireOp",EDGE,"E32.MirrorCS");var subQ3=sQuery(id+"F0.wireOp",EDGE,"E21.trimOffspring");var subQ4=sQuery(id+"F0.wireOp",EDGE,"E2");var subQ5=sQuery(id+"F0.wireOp",EDGE,"E31");var subQ6=sQuery(id+"F0.wireOp",EDGE,"E30");var subQ7=sQuery(id+"F0.wireOp",EDGE,"E1");var subQ8=sQuery(id+"F0.wireOp",EDGE,"E0");var subQ9=sQuery(id+"F0.wireOp",EDGE,"E16.trimOffspring");Q42=makeQuery(id+"F10.opChamfer","BLEND_EDGE",EDGE,{"blendedFrom":[makeQuery(id+"F8.boolean.opBoolean","MERGE",EDGE,{"derivedFrom":[makeQuery(id+"F3.opExtrude","SWEPT_EDGE",EDGE,{"disambiguationData":[OSD([subQ8,subQ9])]}),makeQuery(id+"F8.opExtrude","SWEPT_EDGE",EDGE,{"disambiguationData":[OSD([sQuery(id+"F2.wireOp",EDGE,"E41.0.7"),sQuery(id+"F2.wireOp",EDGE,"E41.0.8")])]})]}),makeQuery(id+"F4.boolean.opBoolean","MERGE",FACE,{"derivedFrom":[makeQuery(id+"F3.opExtrude","CAP_FACE",FACE,{"disambiguationData":[OSD([subQ8,subQ7,subQ4,sQuery(id+"F0.wireOp",EDGE,"E3"),sQuery(id+"F0.wireOp",EDGE,"E7"),sQuery(id+"F0.wireOp",EDGE,"E8"),sQuery(id+"F0.wireOp",EDGE,"E14"),sQuery(id+"F0.wireOp",EDGE,"E15.MirrorCS"),subQ9,sQuery(id+"F0.wireOp",EDGE,"E18"),sQuery(id+"F0.wireOp",EDGE,"E19"),sQuery(id+"F0.wireOp",EDGE,"E20.MirrorCS"),subQ3,subQ6,subQ5,subQ2,subQ1,subQ0])],"isStart":true}),makeQuery(id+"F4.opExtrude","CAP_FACE",FACE,{"disambiguationData":[OSD([subQ8,subQ7,subQ6,subQ5])],"isStart":true}),makeQuery(id+"F4.opExtrude","CAP_FACE",FACE,{"disambiguationData":[OSD([subQ4,subQ3,subQ2,subQ1,subQ0])],"isStart":true})]})],"blendedInto":[makeQuery(id+"F4.boolean.opBoolean","MERGE",FACE,{"derivedFrom":[makeQuery(id+"F3.opExtrude","CAP_FACE",FACE,{"disambiguationData":[OSD([subQ8,subQ7,subQ4,sQuery(id+"F0.wireOp",EDGE,"E3"),sQuery(id+"F0.wireOp",EDGE,"E7"),sQuery(id+"F0.wireOp",EDGE,"E8"),sQuery(id+"F0.wireOp",EDGE,"E14"),sQuery(id+"F0.wireOp",EDGE,"E15.MirrorCS"),subQ9,sQuery(id+"F0.wireOp",EDGE,"E18"),sQuery(id+"F0.wireOp",EDGE,"E19"),sQuery(id+"F0.wireOp",EDGE,"E20.MirrorCS"),subQ3,subQ6,subQ5,subQ2,subQ1,subQ0])],"isStart":true}),makeQuery(id+"F4.opExtrude","CAP_FACE",FACE,{"disambiguationData":[OSD([subQ8,subQ7,subQ6,subQ5])],"isStart":true}),makeQuery(id+"F4.opExtrude","CAP_FACE",FACE,{"disambiguationData":[OSD([subQ4,subQ3,subQ2,subQ1,subQ0])],"isStart":true})]})]});}
            var Q43;
            Q43=makeQuery(id+"F3.opExtrude","CAP_EDGE",EDGE,{"disambiguationData":[OSD([sQuery(id+"F0.wireOp",EDGE,"E16.trimOffspring")])],"isStart":true});
            var Q44;
            Q44=makeQuery(id+"F3.opExtrude","CAP_EDGE",EDGE,{"disambiguationData":[OSD([sQuery(id+"F0.wireOp",EDGE,"E14")])],"isStart":true});
            var Q45;
            {var subQ0=sQuery(id+"F0.wireOp",EDGE,"E34");var subQ1=sQuery(id+"F0.wireOp",EDGE,"E33.MirrorC");var subQ2=sQuery(id+"F0.wireOp",EDGE,"E32.MirrorCS");var subQ3=sQuery(id+"F0.wireOp",EDGE,"E21.trimOffspring");var subQ4=sQuery(id+"F0.wireOp",EDGE,"E2");var subQ5=sQuery(id+"F0.wireOp",EDGE,"E31");var subQ6=sQuery(id+"F0.wireOp",EDGE,"E30");var subQ7=sQuery(id+"F0.wireOp",EDGE,"E1");var subQ8=sQuery(id+"F0.wireOp",EDGE,"E0");var subQ9=sQuery(id+"F0.wireOp",EDGE,"E3");Q45=makeQuery(id+"F10.opChamfer","BLEND_EDGE",EDGE,{"blendedFrom":[makeQuery(id+"F8.boolean.opBoolean","MERGE",EDGE,{"derivedFrom":[makeQuery(id+"F3.opExtrude","SWEPT_EDGE",EDGE,{"disambiguationData":[OSD([subQ4,subQ9])]}),makeQuery(id+"F8.opExtrude","SWEPT_EDGE",EDGE,{"disambiguationData":[OSD([sQuery(id+"F2.wireOp",EDGE,"E41.0.2"),sQuery(id+"F2.wireOp",EDGE,"E41.0.3")])]})]}),makeQuery(id+"F4.boolean.opBoolean","MERGE",FACE,{"derivedFrom":[makeQuery(id+"F3.opExtrude","CAP_FACE",FACE,{"disambiguationData":[OSD([subQ8,subQ7,subQ4,subQ9,sQuery(id+"F0.wireOp",EDGE,"E7"),sQuery(id+"F0.wireOp",EDGE,"E8"),sQuery(id+"F0.wireOp",EDGE,"E14"),sQuery(id+"F0.wireOp",EDGE,"E15.MirrorCS"),sQuery(id+"F0.wireOp",EDGE,"E16.trimOffspring"),sQuery(id+"F0.wireOp",EDGE,"E18"),sQuery(id+"F0.wireOp",EDGE,"E19"),sQuery(id+"F0.wireOp",EDGE,"E20.MirrorCS"),subQ3,subQ6,subQ5,subQ2,subQ1,subQ0])],"isStart":true}),makeQuery(id+"F4.opExtrude","CAP_FACE",FACE,{"disambiguationData":[OSD([subQ8,subQ7,subQ6,subQ5])],"isStart":true}),makeQuery(id+"F4.opExtrude","CAP_FACE",FACE,{"disambiguationData":[OSD([subQ4,subQ3,subQ2,subQ1,subQ0])],"isStart":true})]})],"blendedInto":[makeQuery(id+"F4.boolean.opBoolean","MERGE",FACE,{"derivedFrom":[makeQuery(id+"F3.opExtrude","CAP_FACE",FACE,{"disambiguationData":[OSD([subQ8,subQ7,subQ4,subQ9,sQuery(id+"F0.wireOp",EDGE,"E7"),sQuery(id+"F0.wireOp",EDGE,"E8"),sQuery(id+"F0.wireOp",EDGE,"E14"),sQuery(id+"F0.wireOp",EDGE,"E15.MirrorCS"),sQuery(id+"F0.wireOp",EDGE,"E16.trimOffspring"),sQuery(id+"F0.wireOp",EDGE,"E18"),sQuery(id+"F0.wireOp",EDGE,"E19"),sQuery(id+"F0.wireOp",EDGE,"E20.MirrorCS"),subQ3,subQ6,subQ5,subQ2,subQ1,subQ0])],"isStart":true}),makeQuery(id+"F4.opExtrude","CAP_FACE",FACE,{"disambiguationData":[OSD([subQ8,subQ7,subQ6,subQ5])],"isStart":true}),makeQuery(id+"F4.opExtrude","CAP_FACE",FACE,{"disambiguationData":[OSD([subQ4,subQ3,subQ2,subQ1,subQ0])],"isStart":true})]})]});}
            var Q46;
            Q46=makeQuery(id+"F3.opExtrude","CAP_EDGE",EDGE,{"disambiguationData":[OSD([sQuery(id+"F0.wireOp",EDGE,"E3")])],"isStart":true});
            var Q47;
            Q47=makeQuery(id+"F6.boolean.opBoolean","COPY",EDGE,{"derivedFrom":makeQuery(id+"F6.opExtrude","CAP_EDGE",EDGE,{"disambiguationData":[OSD([sQuery(id+"F2.wireOp",EDGE,"E40.0")])],"isStart":true})});
            fillet(context, id + "F11", {"entities" : qUnion([Q0, Q1, Q2, Q3, Q4, Q5, Q6, Q7, Q8, Q9, Q10, Q11, Q12, Q13, Q14, Q15, Q16, Q17, Q18, Q19, Q20, Q21, Q22, Q23, Q24, Q25, Q26, Q27, Q28, Q29, Q30, Q31, Q32, Q33, Q34, Q35, Q36, Q37, Q38, Q39, Q40, Q41, Q42, Q43, Q44, Q45, Q46, Q47]), "radius" : .2 * mm, "tangentPropagation" : true, "allowEdgeOverflow" : false});
        }
    });
